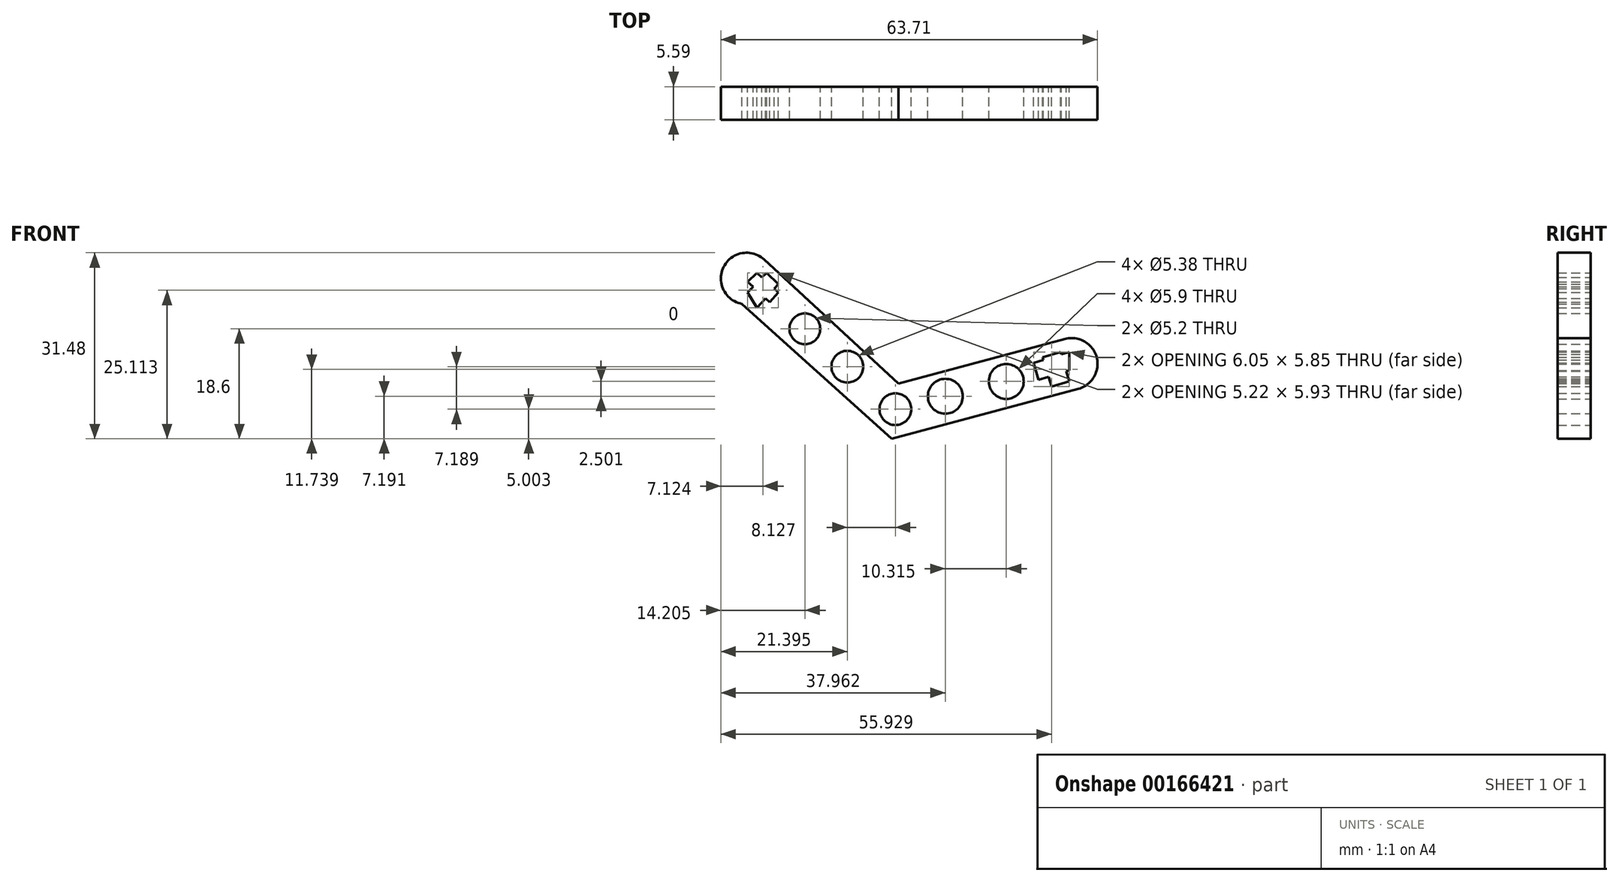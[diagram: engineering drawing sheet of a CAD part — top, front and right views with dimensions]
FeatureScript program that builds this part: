
annotation { "Feature Type Name" : "Feature", "Feature Type Description" : "" }
export const myFeature = defineFeature(function(context is Context, id is Id, definition is map)
    precondition{}
    {
        {
            var Q0;
            Q0=qCreatedBy(makeId("Front.planeOp"),FACE);
            var sketch = newSketch(context, id + "F0", { "sketchPlane" : qUnion([Q0])});
            skLineSegment(sketch, "E0", {"start": v(-37.82, 4.22) * mm, "end": v(-12.5, -18.6) * mm});
            skLineSegment(sketch, "E1", {"start": v(-12.5, -18.6) * mm, "end": v(19.07, -10.16) * mm});
            skLineSegment(sketch, "E2", {"start": v(19.07, -10.16) * mm, "end": v(16.81, -1.72) * mm});
            skLineSegment(sketch, "E3", {"start": v(16.81, -1.72) * mm, "end": v(-11.37, -9.25) * mm});
            skLineSegment(sketch, "E4", {"start": v(-11.37, -9.25) * mm, "end": v(-34.07, 11.72) * mm});
            skLineSegment(sketch, "E5", {"start": v(-34.07, 11.72) * mm, "end": v(-37.82, 4.22) * mm});
            skCircle(sketch, "E6", {"center": v(-27.2, 0) * mm, "radius": 2.6 * mm});
            skCircle(sketch, "E7", {"center": v(-20, -6.4) * mm, "radius": 2.69 * mm});
            skCircle(sketch, "E8", {"center": v(-3.44, -11.4) * mm, "radius": 2.95 * mm});
            skCircle(sketch, "E9", {"center": v(6.88, -8.9) * mm, "radius": 2.95 * mm});
            skCircle(sketch, "E10", {"center": v(-11.88, -13.6) * mm, "radius": 2.69 * mm});
            skArc(sketch, "E11", {"start": v(19.07, -10.16) * mm, "mid": v(22.16, -4.8) * mm, "end": v(16.81, -1.72) * mm});
            skArc(sketch, "E12", {"start": v(-34.07, 11.72) * mm, "mid": v(-40.94, 10.47) * mm, "end": v(-37.82, 4.22) * mm});
            skSolve(sketch);
        }
        {
            var Q0;
            Q0=makeQuery(id+"F0.imprint","IMPRINT",FACE,{"disambiguationData":[TD([[makeQuery(id+"F0.imprint","IMPRINT",EDGE,{"derivedFrom":sQuery(id+"F0.wireOp",EDGE,"E5")}),-1.0]])]});
            var Q1;
            Q1=makeQuery(id+"F0.imprint","IMPRINT",FACE,{"disambiguationData":[TD([[makeQuery(id+"F0.imprint","IMPRINT",EDGE,{"derivedFrom":sQuery(id+"F0.wireOp",EDGE,"E0")}),1.0]])]});
            var Q2;
            Q2=makeQuery(id+"F0.imprint","IMPRINT",FACE,{"disambiguationData":[TD([[makeQuery(id+"F0.imprint","IMPRINT",EDGE,{"derivedFrom":sQuery(id+"F0.wireOp",EDGE,"E2")}),-1.0]])]});
            extrude(context, id + "F1", {"entities" : qUnion([Q0, Q1, Q2]), "depth" : 5.6 * mm});
        }
        {
            var Q0;
            Q0=qCreatedBy(makeId("Front.planeOp"),FACE);
            var sketch = newSketch(context, id + "F2", { "sketchPlane" : qUnion([Q0])});
            skLineSegment(sketch, "E13", {"start": v(-36.88, 7.97) * mm, "end": v(-33.13, 4.53) * mm});
            skLineSegment(sketch, "E14", {"start": v(-33.13, 4.53) * mm, "end": v(-31.67, 6.13) * mm});
            skLineSegment(sketch, "E15", {"start": v(-31.67, 6.13) * mm, "end": v(-35.32, 9.48) * mm});
            skLineSegment(sketch, "E16", {"start": v(-36.88, 7.97) * mm, "end": v(-35.32, 9.48) * mm});
            skLineSegment(sketch, "E17", {"start": v(-33.67, 7.97) * mm, "end": v(-35.32, 6.18) * mm});
            skLineSegment(sketch, "E18", {"start": v(-35.32, 6.18) * mm, "end": v(-33.67, 7.97) * mm});
            skLineSegment(sketch, "E19", {"start": v(-36.88, 6.18) * mm, "end": v(-33.67, 9.48) * mm});
            skLineSegment(sketch, "E20", {"start": v(-33.67, 9.48) * mm, "end": v(-31.67, 7.53) * mm});
            skLineSegment(sketch, "E21", {"start": v(-31.67, 7.53) * mm, "end": v(-35.32, 3.55) * mm});
            skLineSegment(sketch, "E22", {"start": v(-35.32, 3.55) * mm, "end": v(-36.88, 6.18) * mm});
            skLineSegment(sketch, "E23", {"start": v(11.5, -5.75) * mm, "end": v(17.56, -3.93) * mm});
            skLineSegment(sketch, "E24", {"start": v(11.5, -5.75) * mm, "end": v(12.36, -8.6) * mm});
            skLineSegment(sketch, "E25", {"start": v(12.36, -8.6) * mm, "end": v(17.56, -7.04) * mm});
            skLineSegment(sketch, "E26", {"start": v(17.56, -7.04) * mm, "end": v(17.56, -3.93) * mm});
            skLineSegment(sketch, "E27", {"start": v(14.53, -9.79) * mm, "end": v(13.05, -4.84) * mm});
            skPoint(sketch, "E27.startSnap0", {"position": v(14.53, -4.84) * mm});
            skPoint(sketch, "E27.endSnap0", {"position": v(14.53, -4.84) * mm});
            skLineSegment(sketch, "E28", {"start": v(13.05, -4.84) * mm, "end": v(16.07, -3.93) * mm});
            skLineSegment(sketch, "E29", {"start": v(16.07, -3.93) * mm, "end": v(17.56, -8.88) * mm});
            skLineSegment(sketch, "E30", {"start": v(17.56, -8.88) * mm, "end": v(14.53, -9.79) * mm});
            skSolve(sketch);
        }
        {
            var Q0;
            Q0 = qSketchRegion(id + "F2", true);
            extrude(context, id + "F3", {"entities" : qUnion([Q0]), "operationType" : NewBodyOperationType.REMOVE, "depth" : 25.4 * mm});
        }
    });
